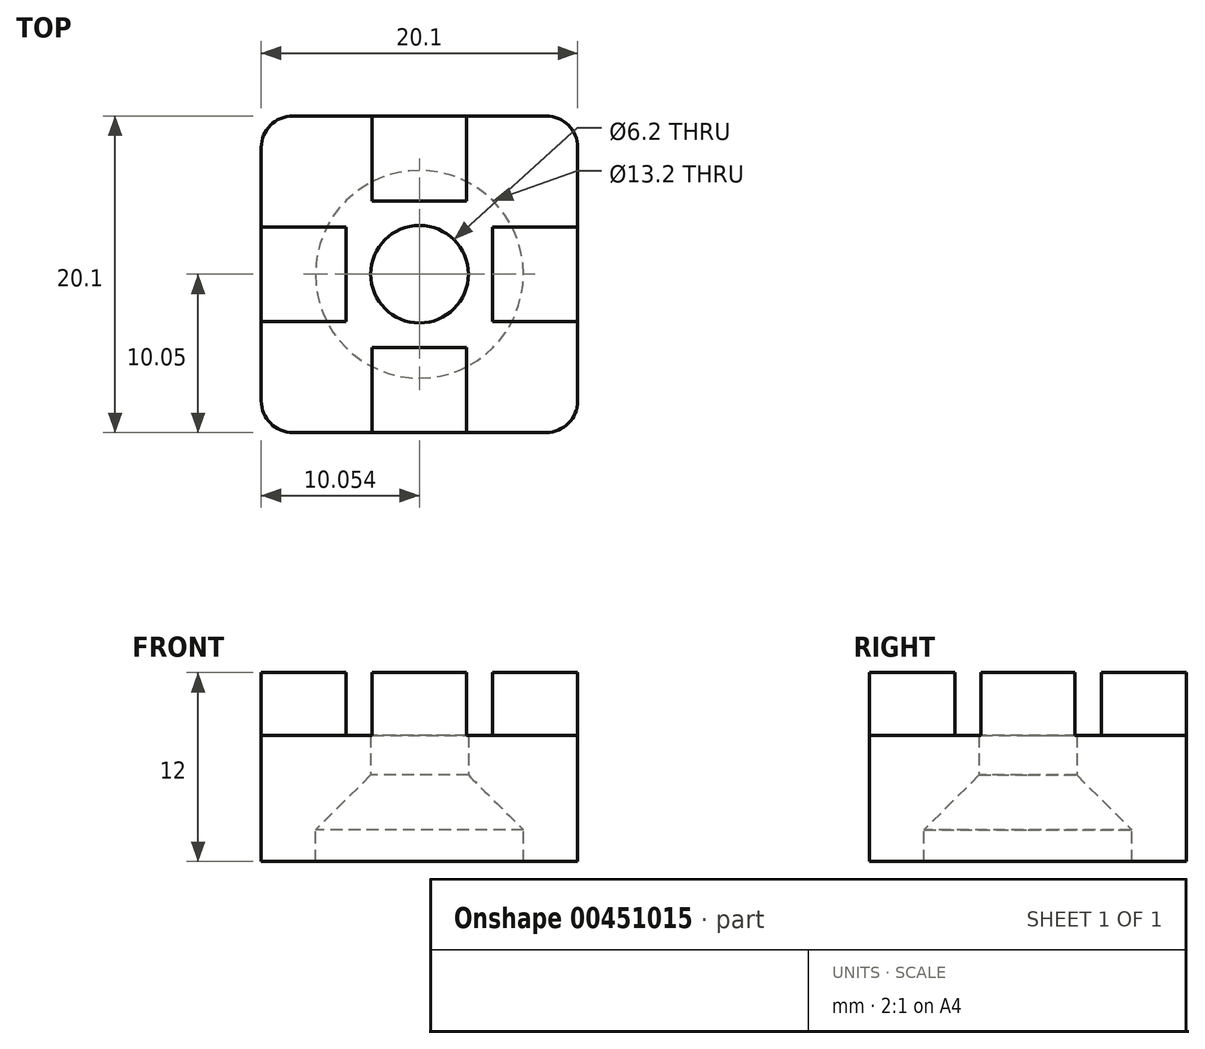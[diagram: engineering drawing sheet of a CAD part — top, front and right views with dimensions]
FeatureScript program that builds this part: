
annotation { "Feature Type Name" : "Feature", "Feature Type Description" : "" }
export const myFeature = defineFeature(function(context is Context, id is Id, definition is map)
    precondition{}
    {
        {
            var Q0;
            Q0=qCreatedBy(makeId("Top.planeOp"),FACE);
            var sketch = newSketch(context, id + "F0", { "sketchPlane" : qUnion([Q0])});
            skLineSegment(sketch, "E0.bottom", {"start": v(-8, 0) * mm, "end": v(12.1, 0) * mm});
            skLineSegment(sketch, "E0.top", {"start": v(-8, 20.1) * mm, "end": v(12.1, 20.1) * mm});
            skLineSegment(sketch, "E0.left", {"start": v(-8, 0) * mm, "end": v(-8, 20.1) * mm});
            skLineSegment(sketch, "E0.right", {"start": v(12.1, 0) * mm, "end": v(12.1, 20.1) * mm});
            skPoint(sketch, "E1", {"position": v(2.05, 20.1) * mm});
            skPoint(sketch, "E2", {"position": v(12.1, 10.05) * mm});
            skLineSegment(sketch, "E3.bottom", {"start": v(-0.95, 20.1) * mm, "end": v(5.05, 20.1) * mm});
            skLineSegment(sketch, "E3.top", {"start": v(-0.95, 14.7) * mm, "end": v(5.05, 14.7) * mm});
            skLineSegment(sketch, "E3.left", {"start": v(-0.95, 20.1) * mm, "end": v(-0.95, 14.7) * mm});
            skLineSegment(sketch, "E3.right", {"start": v(5.05, 20.1) * mm, "end": v(5.05, 14.7) * mm});
            skLineSegment(sketch, "E4.bottom", {"start": v(-0.95, 0) * mm, "end": v(5.05, 0) * mm});
            skLineSegment(sketch, "E4.top", {"start": v(-0.95, 5.4) * mm, "end": v(5.05, 5.4) * mm});
            skLineSegment(sketch, "E4.left", {"start": v(-0.95, 0) * mm, "end": v(-0.95, 5.4) * mm});
            skLineSegment(sketch, "E4.right", {"start": v(5.05, 0) * mm, "end": v(5.05, 5.4) * mm});
            skLineSegment(sketch, "E5.bottom", {"start": v(-8, 13.05) * mm, "end": v(-2.6, 13.05) * mm});
            skLineSegment(sketch, "E5.top", {"start": v(-8, 7.05) * mm, "end": v(-2.6, 7.05) * mm});
            skLineSegment(sketch, "E5.left", {"start": v(-8, 13.05) * mm, "end": v(-8, 7.05) * mm});
            skLineSegment(sketch, "E5.right", {"start": v(-2.6, 13.05) * mm, "end": v(-2.6, 7.05) * mm});
            skLineSegment(sketch, "E6.bottom", {"start": v(12.1, 13.05) * mm, "end": v(6.7, 13.05) * mm});
            skLineSegment(sketch, "E6.top", {"start": v(12.1, 7.05) * mm, "end": v(6.7, 7.05) * mm});
            skLineSegment(sketch, "E6.left", {"start": v(12.1, 13.05) * mm, "end": v(12.1, 7.05) * mm});
            skLineSegment(sketch, "E6.right", {"start": v(6.7, 13.05) * mm, "end": v(6.7, 7.05) * mm});
            skPoint(sketch, "E7", {"position": v(2.05, 14.7) * mm});
            skPoint(sketch, "E8", {"position": v(6.7, 10.05) * mm});
            skCircle(sketch, "E9", {"center": v(2.05, 10.05) * mm, "radius": 3.1 * mm});
            skPoint(sketch, "E9.centerSnap0", {"position": v(-2.6, 10.05) * mm});
            skSolve(sketch);
        }
        {
            var Q0;
            Q0=makeQuery(id+"F0.imprint","IMPRINT",FACE,{"disambiguationData":[TD([[makeQuery(id+"F0.imprint","IMPRINT",EDGE,{"derivedFrom":sQuery(id+"F0.wireOp",EDGE,"E3.top")}),-1.0]])]});
            var Q1;
            Q1=makeQuery(id+"F0.imprint","IMPRINT",FACE,{"disambiguationData":[TD([[makeQuery(id+"F0.imprint","IMPRINT",EDGE,{"derivedFrom":sQuery(id+"F0.wireOp",EDGE,"E3.top")}),-1.0]])]});
            var Q2;
            Q2=makeQuery(id+"F0.imprint","IMPRINT",FACE,{"disambiguationData":[TD([[makeQuery(id+"F0.imprint","IMPRINT",EDGE,{"derivedFrom":sQuery(id+"F0.wireOp",EDGE,"E3.top")}),-1.0]])]});
            var Q3;
            {var subQ0=sQuery(id+"F0.wireOp",EDGE,"E6.bottom");Q3=makeQuery(id+"F0.imprint","IMPRINT",FACE,{"disambiguationData":[TD([[makeQuery(id+"F0.imprint","IMPRINT",EDGE,{"derivedFrom":subQ0}),1.0]])]});}
            var Q4;
            {var subQ0=sQuery(id+"F0.wireOp",EDGE,"E5.bottom");Q4=makeQuery(id+"F0.imprint","IMPRINT",FACE,{"disambiguationData":[TD([[makeQuery(id+"F0.imprint","IMPRINT",EDGE,{"derivedFrom":subQ0}),-1.0]])]});}
            var Q5;
            Q5=makeQuery(id+"F0.imprint","IMPRINT",FACE,{"disambiguationData":[TD([[makeQuery(id+"F0.imprint","IMPRINT",EDGE,{"derivedFrom":sQuery(id+"F0.wireOp",EDGE,"E3.top")}),1.0]])]});
            var Q6;
            Q6=makeQuery(id+"F0.imprint","IMPRINT",FACE,{"disambiguationData":[TD([[makeQuery(id+"F0.imprint","IMPRINT",EDGE,{"derivedFrom":sQuery(id+"F0.wireOp",EDGE,"E4.top")}),-1.0]])]});
            var Q7;
            Q7=makeQuery(id+"F0.imprint","IMPRINT",FACE,{"disambiguationData":[TD([[makeQuery(id+"F0.imprint","IMPRINT",EDGE,{"derivedFrom":sQuery(id+"F0.wireOp",EDGE,"E3.top")}),1.0]])]});
            var Q8;
            Q8=makeQuery(id+"F0.imprint","IMPRINT",FACE,{"disambiguationData":[TD([[makeQuery(id+"F0.imprint","IMPRINT",EDGE,{"derivedFrom":sQuery(id+"F0.wireOp",EDGE,"E3.top")}),-1.0]])]});
            var Q9;
            {var subQ0=sQuery(id+"F0.wireOp",EDGE,"E5.bottom");Q9=makeQuery(id+"F0.imprint","IMPRINT",FACE,{"disambiguationData":[TD([[makeQuery(id+"F0.imprint","IMPRINT",EDGE,{"derivedFrom":subQ0}),-1.0]])]});}
            var Q10;
            Q10=makeQuery(id+"F0.imprint","IMPRINT",FACE,{"disambiguationData":[TD([[makeQuery(id+"F0.imprint","IMPRINT",EDGE,{"derivedFrom":sQuery(id+"F0.wireOp",EDGE,"E4.top")}),-1.0]])]});
            var Q11;
            {var subQ0=sQuery(id+"F0.wireOp",EDGE,"E6.bottom");Q11=makeQuery(id+"F0.imprint","IMPRINT",FACE,{"disambiguationData":[TD([[makeQuery(id+"F0.imprint","IMPRINT",EDGE,{"derivedFrom":subQ0}),1.0]])]});}
            extrude(context, id + "F1", {"entities" : qUnion([Q0, Q1, Q2, Q3, Q4, Q5, Q6, Q7, Q8, Q9, Q10, Q11]), "depth" : 6 * mm});
        }
        {
            var Q0;
            Q0=makeQuery(id+"F0.imprint","IMPRINT",FACE,{"disambiguationData":[TD([[makeQuery(id+"F0.imprint","IMPRINT",EDGE,{"derivedFrom":sQuery(id+"F0.wireOp",EDGE,"E3.top")}),1.0]])]});
            var Q1;
            {var subQ0=sQuery(id+"F0.wireOp",EDGE,"E5.bottom");Q1=makeQuery(id+"F0.imprint","IMPRINT",FACE,{"disambiguationData":[TD([[makeQuery(id+"F0.imprint","IMPRINT",EDGE,{"derivedFrom":subQ0}),-1.0]])]});}
            var Q2;
            Q2=makeQuery(id+"F0.imprint","IMPRINT",FACE,{"disambiguationData":[TD([[makeQuery(id+"F0.imprint","IMPRINT",EDGE,{"derivedFrom":sQuery(id+"F0.wireOp",EDGE,"E4.top")}),-1.0]])]});
            var Q3;
            {var subQ0=sQuery(id+"F0.wireOp",EDGE,"E6.bottom");Q3=makeQuery(id+"F0.imprint","IMPRINT",FACE,{"disambiguationData":[TD([[makeQuery(id+"F0.imprint","IMPRINT",EDGE,{"derivedFrom":subQ0}),1.0]])]});}
            extrude(context, id + "F2", {"entities" : qUnion([Q0, Q1, Q2, Q3]), "operationType" : NewBodyOperationType.ADD, "depth" : 10 * mm});
        }
        {
            var Q0;
            Q0=makeQuery(id+"F1.opExtrude","SWEPT_EDGE",EDGE,{"disambiguationData":[OSD([sQuery(id+"F0.wireOp",EDGE,"E0.bottom"),sQuery(id+"F0.wireOp",EDGE,"E0.left")])]});
            var Q1;
            Q1=makeQuery(id+"F1.opExtrude","SWEPT_EDGE",EDGE,{"disambiguationData":[OSD([sQuery(id+"F0.wireOp",EDGE,"E0.bottom"),sQuery(id+"F0.wireOp",EDGE,"E0.right")])]});
            var Q2;
            Q2=makeQuery(id+"F1.opExtrude","SWEPT_EDGE",EDGE,{"disambiguationData":[OSD([sQuery(id+"F0.wireOp",EDGE,"E0.top"),sQuery(id+"F0.wireOp",EDGE,"E0.right")])]});
            var Q3;
            Q3=makeQuery(id+"F1.opExtrude","SWEPT_EDGE",EDGE,{"disambiguationData":[OSD([sQuery(id+"F0.wireOp",EDGE,"E0.top"),sQuery(id+"F0.wireOp",EDGE,"E0.left")])]});
            fillet(context, id + "F3", {"entities" : qUnion([Q0, Q1, Q2, Q3]), "radius" : 2 * mm, "tangentPropagation" : true, "allowEdgeOverflow" : false});
        }
        {
            var Q0;
            Q0=makeQuery(id+"F1.opExtrude","CAP_EDGE",EDGE,{"disambiguationData":[OSD([sQuery(id+"F0.wireOp",EDGE,"E9")])],"isStart":true});
            chamfer(context, id + "F4", {"entities" : qUnion([Q0]), "width" : 3.5 * mm, "tangentPropagation" : true});
        }
        {
            var Q0;
            Q0=makeQuery(id+"F1.opExtrude","CAP_FACE",FACE,{"disambiguationData":[OSD([sQuery(id+"F0.wireOp",EDGE,"E0.bottom"),sQuery(id+"F0.wireOp",EDGE,"E0.top"),sQuery(id+"F0.wireOp",EDGE,"E0.left"),sQuery(id+"F0.wireOp",EDGE,"E0.right"),sQuery(id+"F0.wireOp",EDGE,"E9")])],"isStart":true});
            extrude(context, id + "F5", {"entities" : qUnion([Q0]), "operationType" : NewBodyOperationType.ADD, "depth" : 2 * mm});
        }
    });
